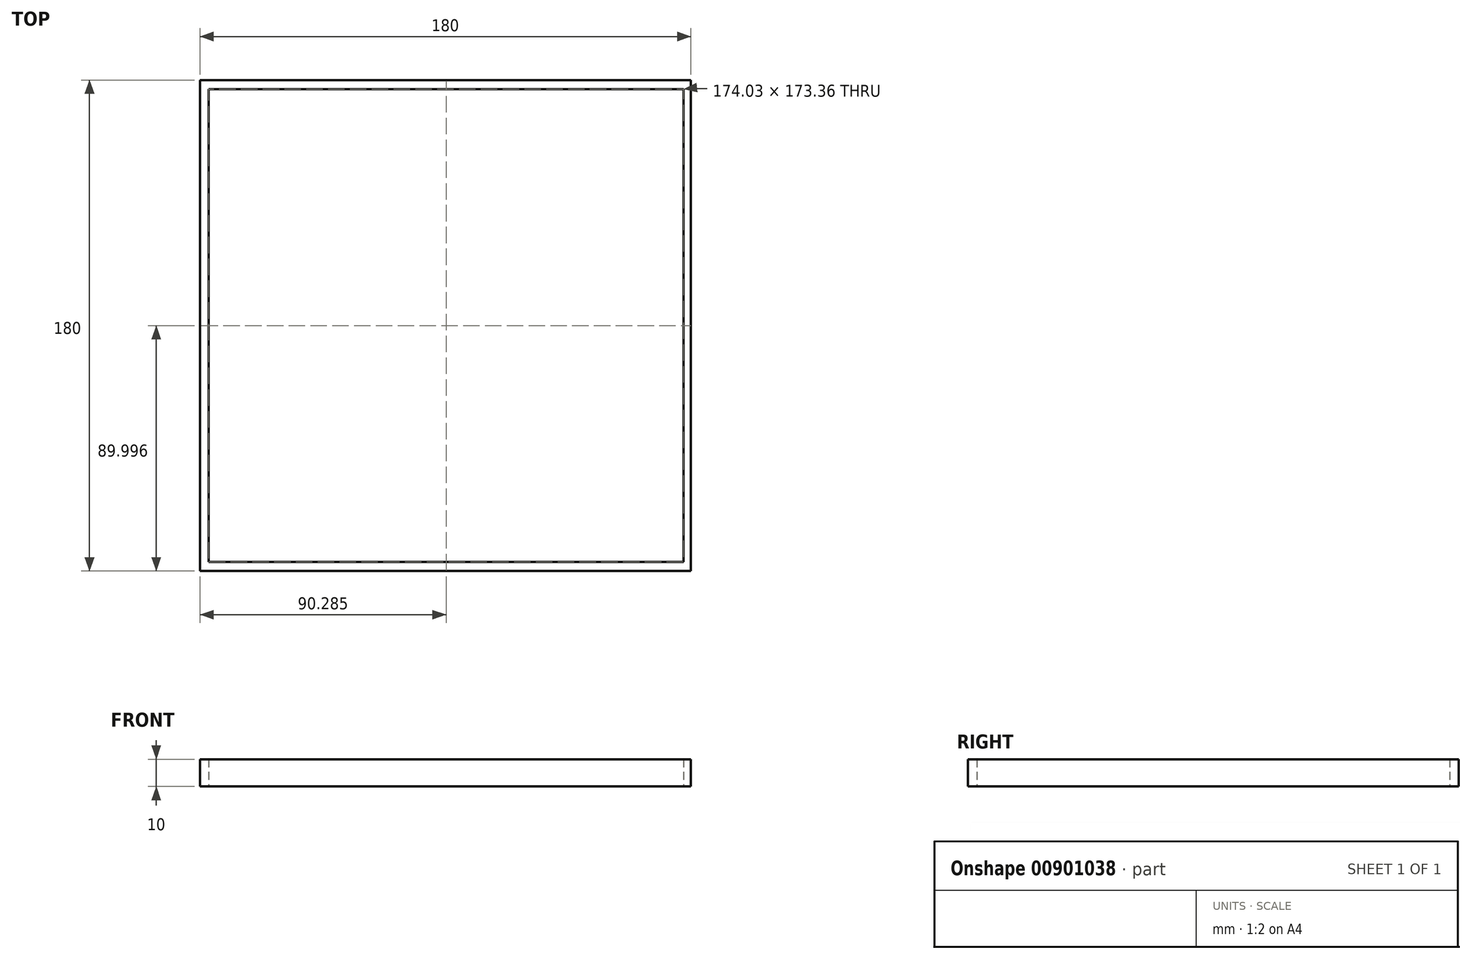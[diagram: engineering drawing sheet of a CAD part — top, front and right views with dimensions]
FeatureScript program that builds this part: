
annotation { "Feature Type Name" : "Feature", "Feature Type Description" : "" }
export const myFeature = defineFeature(function(context is Context, id is Id, definition is map)
    precondition{}
    {
        {
            var Q0;
            Q0=qCreatedBy(makeId("Top.planeOp"),FACE);
            var sketch = newSketch(context, id + "F0", { "sketchPlane" : qUnion([Q0])});
            skLineSegment(sketch, "E0.bottom", {"start": v(-110.12, 104.72) * mm, "end": v(69.88, 104.72) * mm});
            skLineSegment(sketch, "E0.top", {"start": v(-110.12, -75.28) * mm, "end": v(69.88, -75.28) * mm});
            skLineSegment(sketch, "E0.left", {"start": v(-110.12, 104.72) * mm, "end": v(-110.12, -75.28) * mm});
            skLineSegment(sketch, "E0.right", {"start": v(69.88, 104.72) * mm, "end": v(69.88, -75.28) * mm});
            skLineSegment(sketch, "E1.bottom", {"start": v(-106.85, -71.96) * mm, "end": v(67.18, -71.96) * mm});
            skLineSegment(sketch, "E1.top", {"start": v(-106.85, 101.4) * mm, "end": v(67.18, 101.4) * mm});
            skLineSegment(sketch, "E1.left", {"start": v(-106.85, -71.96) * mm, "end": v(-106.85, 101.4) * mm});
            skLineSegment(sketch, "E1.right", {"start": v(67.18, -71.96) * mm, "end": v(67.18, 101.4) * mm});
            skSolve(sketch);
        }
        {
            var Q0;
            Q0 = qSketchRegion(id + "F0", true);
            extrude(context, id + "F1", {"entities" : qUnion([Q0]), "depth" : 10 * mm, "offsetDistance" : 25 * mm});
        }
    });
